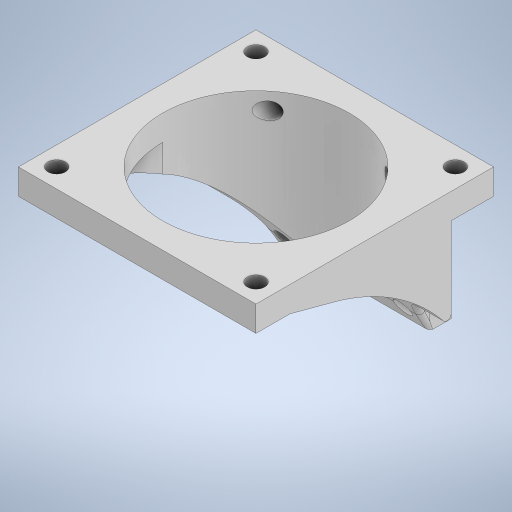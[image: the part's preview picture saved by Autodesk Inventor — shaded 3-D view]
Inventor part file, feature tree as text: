
AUTODESK INVENTOR PART (.ipt)
format: ipt  version: 2024 (Build 280153000, 153)  size: 376,320 bytes
history: native  units: mm
features: extrude x4, sketch x4, fillet x3, projected_geometry x2
ambient origin geometry x8: Origin, YZ Plane, XZ Plane, XY Plane, X Axis, Y Axis, Z Axis, Center Point
bodies: Solid1 (feature_tree)
feature tree (13):
  extrude  "Extrusion1"  Depth=56.0mm
  extrude  "Extrusion2"  Depth=44.0mm
  extrude  "Extrusion3"  Depth=4.1mm
  fillet  "Fillet1"  Radius=4.1mm
  fillet  "Fillet2"  Radius=4.1mm
  fillet  "Fillet3"  Radius=6.0mm
  extrude  "Extrusion4"  Depth=10.0mm
  sketch  "Sketch1"  dims[d0=56.0mm d1=56.0mm]
  sketch  "Sketch2"  dims[d2=4.5mm d3=44.0mm]
  projected_geometry  "Projected Loop1"
  sketch  "Sketch3"  dims[d4=4.1mm d5=4.1mm d6=4.1mm d7=4.1mm d8=6.0mm d9=0.0mm]
  sketch  "Sketch4"  dims[d10=10.0mm d11=10.0mm d12=10.0mm d13=30.0mm d14=0.0mm d15=23.0mm d16=99.0mm d17=0.0mm d18=50.0mm d19=5.0mm d20=1.0mm d21=35.0mm d22=0.0mm]
  projected_geometry  "Projected Loop2"
